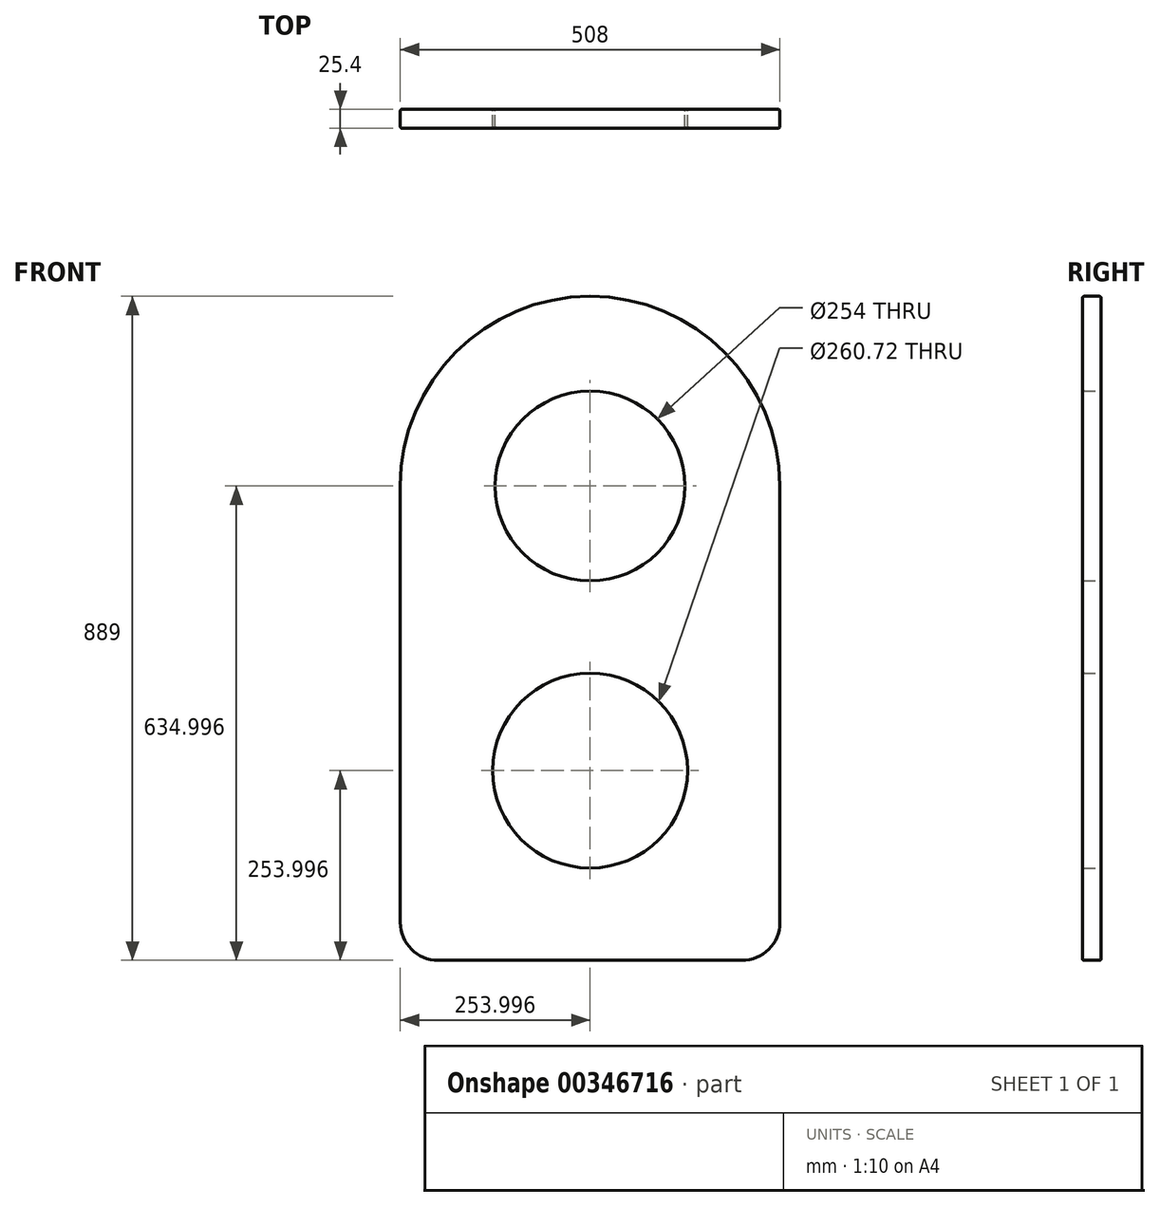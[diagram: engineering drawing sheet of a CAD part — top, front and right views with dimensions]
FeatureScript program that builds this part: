
annotation { "Feature Type Name" : "Feature", "Feature Type Description" : "" }
export const myFeature = defineFeature(function(context is Context, id is Id, definition is map)
    precondition{}
    {
        {
            var Q0;
            Q0=qCreatedBy(makeId("Front.planeOp"),FACE);
            var sketch = newSketch(context, id + "F0", { "sketchPlane" : qUnion([Q0])});
            skLineSegment(sketch, "E0.bottom", {"start": v(-122.62, 586.33) * mm, "end": v(-122.62, 586.33) * mm});
            skLineSegment(sketch, "E0.top", {"start": v(-325.82, -302.67) * mm, "end": v(80.58, -302.67) * mm});
            skLineSegment(sketch, "E0.left", {"start": v(-376.62, 332.33) * mm, "end": v(-376.62, -251.87) * mm});
            skLineSegment(sketch, "E0.right", {"start": v(131.38, 332.33) * mm, "end": v(131.38, -251.87) * mm});
            skCircle(sketch, "E1", {"center": v(-122.62, 332.33) * mm, "radius": 127 * mm});
            skPoint(sketch, "E2.visualSharp", {"position": v(-376.62, 586.33) * mm});
            skArc(sketch, "E2.filletArc", {"start": v(-122.62, 586.33) * mm, "mid": v(-302.23, 511.93) * mm, "end": v(-376.62, 332.33) * mm});
            skPoint(sketch, "E3.visualSharp", {"position": v(131.38, 586.33) * mm});
            skArc(sketch, "E3.filletArc", {"start": v(131.38, 332.33) * mm, "mid": v(56.98, 511.93) * mm, "end": v(-122.62, 586.33) * mm});
            skPoint(sketch, "E4.visualSharp", {"position": v(131.38, -302.67) * mm});
            skArc(sketch, "E4.filletArc", {"start": v(80.58, -302.67) * mm, "mid": v(116.5, -287.8) * mm, "end": v(131.38, -251.87) * mm});
            skPoint(sketch, "E5.visualSharp", {"position": v(-376.62, -302.67) * mm});
            skArc(sketch, "E5.filletArc", {"start": v(-376.62, -251.87) * mm, "mid": v(-361.74, -287.8) * mm, "end": v(-325.82, -302.67) * mm});
            skCircle(sketch, "E6", {"center": v(-122.62, -48.67) * mm, "radius": 130.36 * mm});
            skSolve(sketch);
        }
        {
            var Q0;
            Q0 = qSketchRegion(id + "F0", true);
            extrude(context, id + "F1", {"entities" : qUnion([Q0]), "depth" : 25.4 * mm});
        }
        {
            var Q0;
            Q0=makeQuery(id+"F1.opExtrude","CAP_EDGE",EDGE,{"disambiguationData":[OSD([sQuery(id+"F0.wireOp",EDGE,"E0.bottom")])],"isStart":false});
            var Q1;
            Q1=makeQuery(id+"F1.opExtrude","CAP_EDGE",EDGE,{"disambiguationData":[OSD([sQuery(id+"F0.wireOp",EDGE,"E0.right")])],"isStart":false});
            var Q2;
            Q2=makeQuery(id+"F1.opExtrude","CAP_EDGE",EDGE,{"disambiguationData":[OSD([sQuery(id+"F0.wireOp",EDGE,"E0.top")])],"isStart":false});
            var Q3;
            Q3=makeQuery(id+"F1.opExtrude","CAP_EDGE",EDGE,{"disambiguationData":[OSD([sQuery(id+"F0.wireOp",EDGE,"E0.left")])],"isStart":false});
            var Q4;
            Q4=makeQuery(id+"F1.opExtrude","CAP_EDGE",EDGE,{"disambiguationData":[OSD([sQuery(id+"F0.wireOp",EDGE,"E2.filletArc")])],"isStart":false});
            var Q5;
            Q5=makeQuery(id+"F1.opExtrude","CAP_EDGE",EDGE,{"disambiguationData":[OSD([sQuery(id+"F0.wireOp",EDGE,"E1")])],"isStart":false});
            var Q6;
            Q6=makeQuery(id+"F1.opExtrude","CAP_EDGE",EDGE,{"disambiguationData":[OSD([sQuery(id+"F0.wireOp",EDGE,"E1")])],"isStart":true});
            var Q7;
            Q7=makeQuery(id+"F1.opExtrude","CAP_EDGE",EDGE,{"disambiguationData":[OSD([sQuery(id+"F0.wireOp",EDGE,"E0.left")])],"isStart":true});
            var Q8;
            Q8=makeQuery(id+"F1.opExtrude","CAP_EDGE",EDGE,{"disambiguationData":[OSD([sQuery(id+"F0.wireOp",EDGE,"E2.filletArc")])],"isStart":true});
            var Q9;
            Q9=makeQuery(id+"F1.opExtrude","CAP_EDGE",EDGE,{"disambiguationData":[OSD([sQuery(id+"F0.wireOp",EDGE,"E0.bottom")])],"isStart":true});
            var Q10;
            Q10=makeQuery(id+"F1.opExtrude","CAP_EDGE",EDGE,{"disambiguationData":[OSD([sQuery(id+"F0.wireOp",EDGE,"E0.right")])],"isStart":true});
            var Q11;
            Q11=makeQuery(id+"F1.opExtrude","CAP_EDGE",EDGE,{"disambiguationData":[OSD([sQuery(id+"F0.wireOp",EDGE,"E0.top")])],"isStart":true});
            var Q12;
            Q12=makeQuery(id+"F1.opExtrude","SWEPT_EDGE",EDGE,{"disambiguationData":[OSD([sQuery(id+"F0.wireOp",EDGE,"E0.top"),sQuery(id+"F0.wireOp",EDGE,"E0.right")])]});
            var Q13;
            Q13=makeQuery(id+"F1.opExtrude","SWEPT_EDGE",EDGE,{"disambiguationData":[OSD([sQuery(id+"F0.wireOp",EDGE,"E0.top"),sQuery(id+"F0.wireOp",EDGE,"E0.left")])]});
            var Q14;
            Q14=makeQuery(id+"F1.opExtrude","SWEPT_EDGE",EDGE,{"disambiguationData":[OSD([sQuery(id+"F0.wireOp",EDGE,"E0.bottom"),sQuery(id+"F0.wireOp",EDGE,"E0.right")])]});
            var Q15;
            Q15=makeQuery(id+"F1.opExtrude","CAP_FACE",FACE,{"disambiguationData":[OSD([sQuery(id+"F0.wireOp",EDGE,"E0.top"),sQuery(id+"F0.wireOp",EDGE,"E0.left"),sQuery(id+"F0.wireOp",EDGE,"E0.right"),sQuery(id+"F0.wireOp",EDGE,"E1"),sQuery(id+"F0.wireOp",EDGE,"E2.filletArc"),sQuery(id+"F0.wireOp",EDGE,"E3.filletArc"),sQuery(id+"F0.wireOp",EDGE,"E4.filletArc"),sQuery(id+"F0.wireOp",EDGE,"E5.filletArc"),sQuery(id+"F0.wireOp",EDGE,"E6")])],"isStart":true});
            var Q16;
            Q16=makeQuery(id+"F1.opExtrude","SWEPT_FACE",FACE,{"disambiguationData":[OSD([sQuery(id+"F0.wireOp",EDGE,"E6")])]});
            var Q17;
            Q17=makeQuery(id+"F1.opExtrude","SWEPT_FACE",FACE,{"disambiguationData":[OSD([sQuery(id+"F0.wireOp",EDGE,"E5.filletArc")])]});
            var Q18;
            Q18=makeQuery(id+"F1.opExtrude","CAP_FACE",FACE,{"disambiguationData":[OSD([sQuery(id+"F0.wireOp",EDGE,"E0.top"),sQuery(id+"F0.wireOp",EDGE,"E0.left"),sQuery(id+"F0.wireOp",EDGE,"E0.right"),sQuery(id+"F0.wireOp",EDGE,"E1"),sQuery(id+"F0.wireOp",EDGE,"E2.filletArc"),sQuery(id+"F0.wireOp",EDGE,"E3.filletArc"),sQuery(id+"F0.wireOp",EDGE,"E4.filletArc"),sQuery(id+"F0.wireOp",EDGE,"E5.filletArc"),sQuery(id+"F0.wireOp",EDGE,"E6")])],"isStart":false});
            fillet(context, id + "F2", {"entities" : qUnion([Q0, Q1, Q2, Q3, Q4, Q5, Q6, Q7, Q8, Q9, Q10, Q11, Q12, Q13, Q14, Q15, Q16, Q17, Q18]), "radius" : 2.54 * mm, "tangentPropagation" : true, "allowEdgeOverflow" : false});
        }
    });
